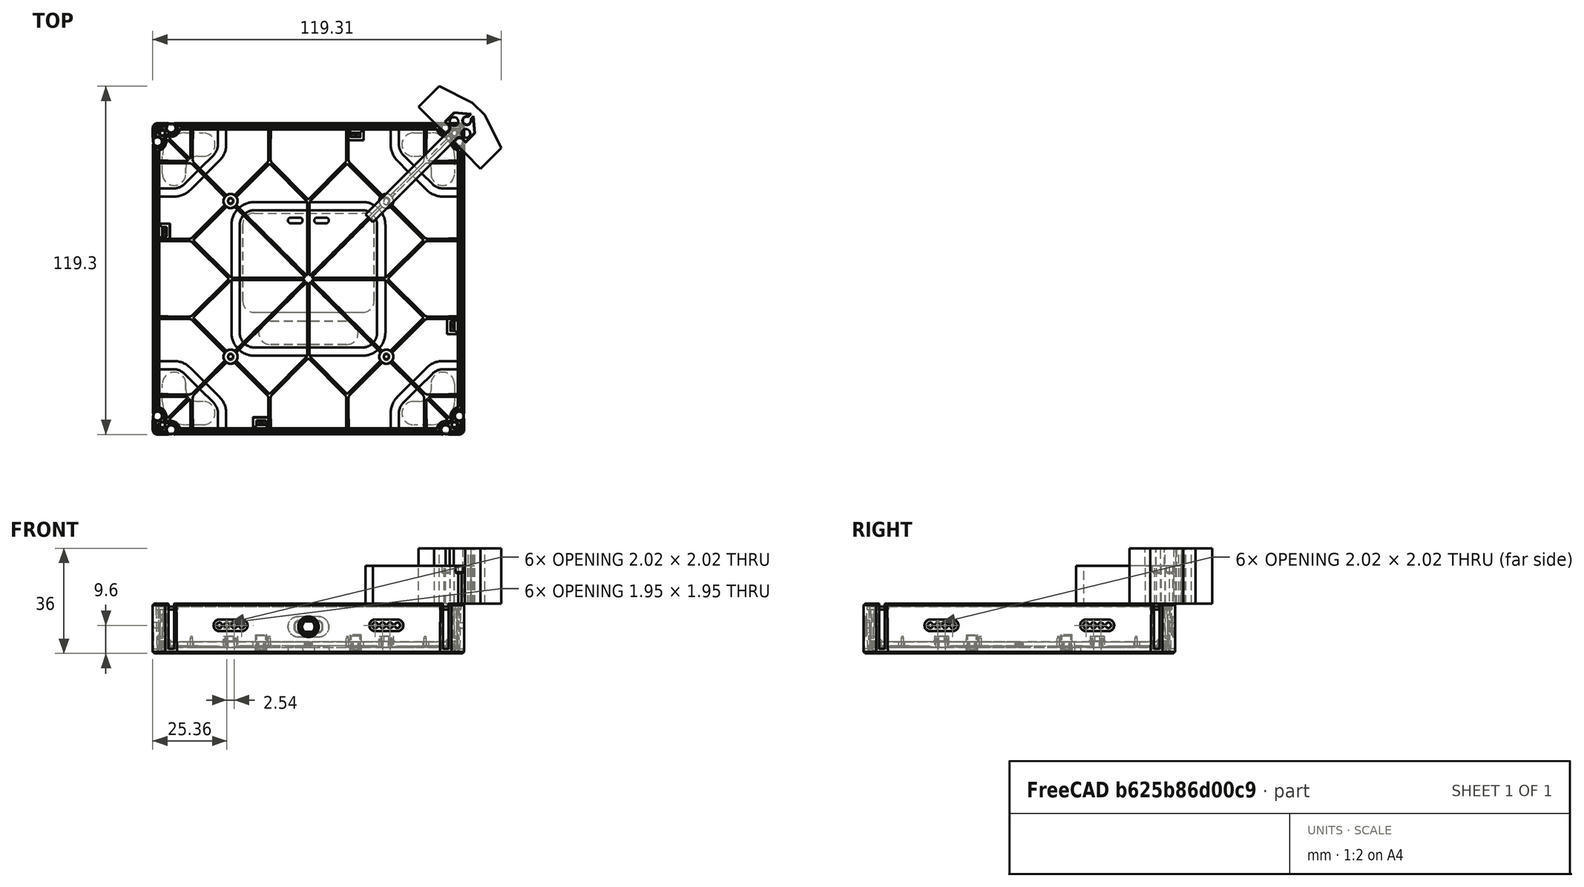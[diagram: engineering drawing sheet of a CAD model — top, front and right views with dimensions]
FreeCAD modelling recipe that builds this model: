
FCSTD DOCUMENT  (FreeCAD 0.21R33771 (Git))
Label: magnet_press_jig_2 part_assy
License: All rights reserved
LicenseURL: https://en.wikipedia.org/wiki/All_rights_reserved
objects: App::FeaturePython×4, Part::FeaturePython×2, Sketcher::SketchObject×1, PartDesign::Body×1
note: 4 computed .brp shape members not serialized (recipe doc carries the construction recipe); baked Part::Feature solids carry a one-line shape summary decoded from their .brp

FEATURE [Part::FeaturePython] b_PLASTIC_CANVAS_001_  label="PLASTIC-CANVAS_001"  # a2plus imported part (geometry in sourceFile) (typed FeaturePython)
  a2p_Version = 0.4.61
  fixedPosition = true
  objectType = a2pPart
  sourceFile = .\..\Mechanical\Design\PLASTIC-CANVAS\PLASTIC-CANVAS.FCStd
  subassemblyImport = false
  timeLastImport = 1.70481e+09
  updateColors = true
FEATURE [Part::FeaturePython] b_magnet_press_jig_side_2_part_001_  label="magnet_press_jig_side_2 part_001"  # a2plus imported part (geometry in sourceFile) (typed FeaturePython)
  Placement = pos=(51.8893,51.88,1.50001) rot=(0,0,-1;0.785398rad)
  a2p_Version = 0.4.61
  fixedPosition = false
  objectType = a2pPart
  sourceFile = .\magnet_press_jig_side_2 part.FCStd
  subassemblyImport = false
  timeLastImport = 1.71688e+09
  updateColors = true
FEATURE [Sketcher::SketchObject] Sketch
  FullyConstrained = true
  MapMode = 5
  Support = -> [XY_Plane]
FEATURE [PartDesign::Body] Body
  Group = -> [Sketch]
  Origin = -> Origin
FEATURE [App::FeaturePython] axisCoincident_001  label="axisCoincident_001__PLASTIC-CANVAS_001"  # a2plus constraint (typed FeaturePython)
  Object1 = b_magnet_press_jig_side_2_part_001_
  Object2 = b_PLASTIC_CANVAS_001_
  ParentTreeObject = -> b_magnet_press_jig_side_2_part_001_
  SubElement1 = Edge95
  SubElement2 = Edge1330
  Suppressed = false
  Type = axial
  directionConstraint = 0
  lockRotation = false
FEATURE [App::FeaturePython] axisCoincident_001_mirror  label="axisCoincident_001__magnet_press_jig_side_2 part_001"  # a2plus constraint (typed FeaturePython)
  Object1 = b_magnet_press_jig_side_2_part_001_
  Object2 = b_PLASTIC_CANVAS_001_
  ParentTreeObject = -> b_PLASTIC_CANVAS_001_
  SubElement1 = Edge95
  SubElement2 = Edge1330
  Suppressed = false
  Type = axial
  directionConstraint = 0
  lockRotation = false
FEATURE [App::FeaturePython] planeCoincident_001  label="planeCoincident_001__PLASTIC-CANVAS_001"  # a2plus constraint (typed FeaturePython)
  Object1 = b_magnet_press_jig_side_2_part_001_
  Object2 = b_PLASTIC_CANVAS_001_
  ParentTreeObject = -> b_magnet_press_jig_side_2_part_001_
  SubElement1 = Face58
  SubElement2 = Face365
  Suppressed = false
  Type = plane
  directionConstraint = 1
  offset = 0
FEATURE [App::FeaturePython] planeCoincident_001_mirror  label="planeCoincident_001__magnet_press_jig_side_2 part_001"  # a2plus constraint (typed FeaturePython)
  Object1 = b_magnet_press_jig_side_2_part_001_
  Object2 = b_PLASTIC_CANVAS_001_
  ParentTreeObject = -> b_PLASTIC_CANVAS_001_
  SubElement1 = Face58
  SubElement2 = Face365
  Suppressed = false
  Type = plane
  directionConstraint = 1
  offset = 0
